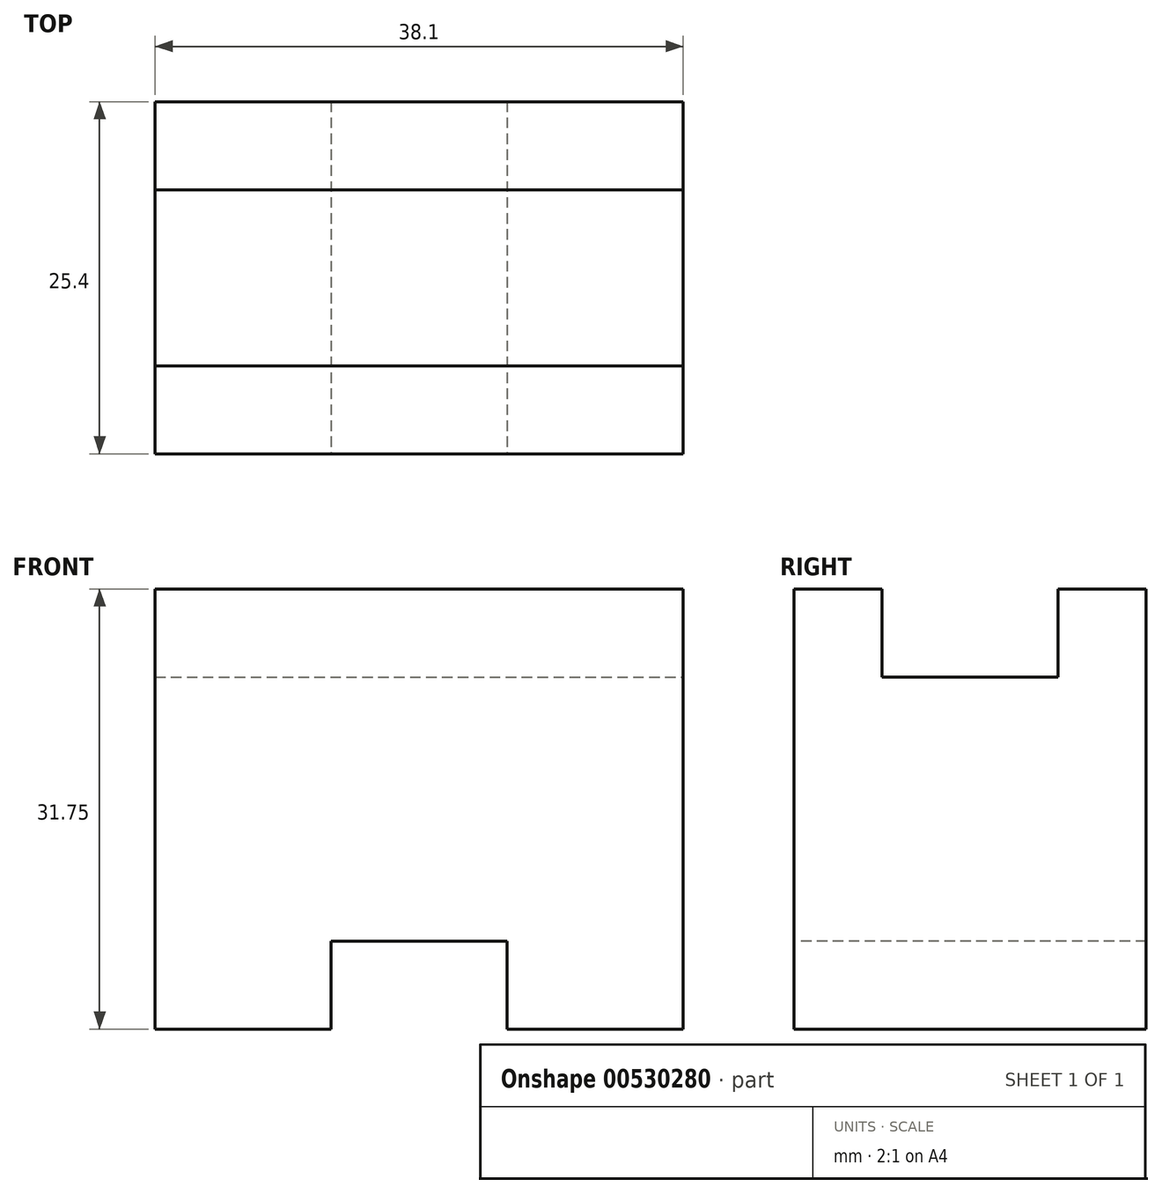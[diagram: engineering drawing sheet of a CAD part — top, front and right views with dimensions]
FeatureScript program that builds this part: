
annotation { "Feature Type Name" : "Feature", "Feature Type Description" : "" }
export const myFeature = defineFeature(function(context is Context, id is Id, definition is map)
    precondition{}
    {
        {
            var Q0;
            Q0=qCreatedBy(makeId("Front.planeOp"),FACE);
            var sketch = newSketch(context, id + "F0", { "sketchPlane" : qUnion([Q0])});
            skLineSegment(sketch, "E0", {"start": v(-52.47, 31.75) * mm, "end": v(-52.47, 0) * mm});
            skLineSegment(sketch, "E1", {"start": v(-52.47, 0) * mm, "end": v(-14.37, 0) * mm});
            skLineSegment(sketch, "E2", {"start": v(-14.37, 0) * mm, "end": v(-14.37, 31.75) * mm});
            skLineSegment(sketch, "E3", {"start": v(-52.47, 31.75) * mm, "end": v(-14.37, 31.75) * mm});
            skSolve(sketch);
        }
        {
            var Q0;
            Q0=makeQuery(id+"F0.imprint","IMPRINT",FACE,{"disambiguationData":[TD([[makeQuery(id+"F0.imprint","IMPRINT",EDGE,{"derivedFrom":sQuery(id+"F0.wireOp",EDGE,"E0")}),1.0]])]});
            extrude(context, id + "F1", {"entities" : qUnion([Q0]), "depth" : 25.4 * mm, "offsetDistance" : 25.4 * mm});
        }
        {
            var Q0;
            Q0=makeQuery(id+"F1.opExtrude","SWEPT_FACE",FACE,{"disambiguationData":[OSD([sQuery(id+"F0.wireOp",EDGE,"E3")])]});
            var sketch = newSketch(context, id + "F2", { "sketchPlane" : qUnion([Q0])});
            skLineSegment(sketch, "E4", {"start": v(-52.47, -19.05) * mm, "end": v(-14.37, -19.05) * mm});
            skLineSegment(sketch, "E5", {"start": v(-14.37, -19.05) * mm, "end": v(-14.37, -6.35) * mm});
            skLineSegment(sketch, "E6", {"start": v(-14.37, -6.35) * mm, "end": v(-52.47, -6.35) * mm});
            skSolve(sketch);
        }
        {
            var Q0;
            {var subQ0=sQuery(id+"F2.wireOp",EDGE,"E4");Q0=makeQuery(id+"F2.imprint","IMPRINT",FACE,{"disambiguationData":[TD([[makeQuery(id+"F2.imprint","IMPRINT",EDGE,{"derivedFrom":subQ0}),1.0]])]});}
            extrude(context, id + "F3", {"entities" : qUnion([Q0]), "operationType" : NewBodyOperationType.REMOVE, "oppositeDirection" : true, "depth" : 6.35 * mm, "offsetDistance" : 25.4 * mm});
        }
        {
            var Q0;
            Q0=makeQuery(id+"F1.opExtrude","CAP_FACE",FACE,{"disambiguationData":[OSD([sQuery(id+"F0.wireOp",EDGE,"E0"),sQuery(id+"F0.wireOp",EDGE,"E1"),sQuery(id+"F0.wireOp",EDGE,"E2"),sQuery(id+"F0.wireOp",EDGE,"E3")])],"isStart":false});
            var sketch = newSketch(context, id + "F4", { "sketchPlane" : qUnion([Q0])});
            skLineSegment(sketch, "E7", {"start": v(-39.77, 0) * mm, "end": v(-39.77, 6.35) * mm});
            skLineSegment(sketch, "E8", {"start": v(-39.77, 6.35) * mm, "end": v(-27.07, 6.35) * mm});
            skLineSegment(sketch, "E9", {"start": v(-27.07, 6.35) * mm, "end": v(-27.07, 0) * mm});
            skSolve(sketch);
        }
        {
            var Q0;
            {var subQ0=sQuery(id+"F4.wireOp",EDGE,"E7");Q0=makeQuery(id+"F4.imprint","IMPRINT",FACE,{"disambiguationData":[TD([[makeQuery(id+"F4.imprint","IMPRINT",EDGE,{"derivedFrom":subQ0}),-1.0]])]});}
            extrude(context, id + "F5", {"entities" : qUnion([Q0]), "operationType" : NewBodyOperationType.REMOVE, "oppositeDirection" : true, "depth" : 38.1 * mm, "offsetDistance" : 25.4 * mm});
        }
    });
